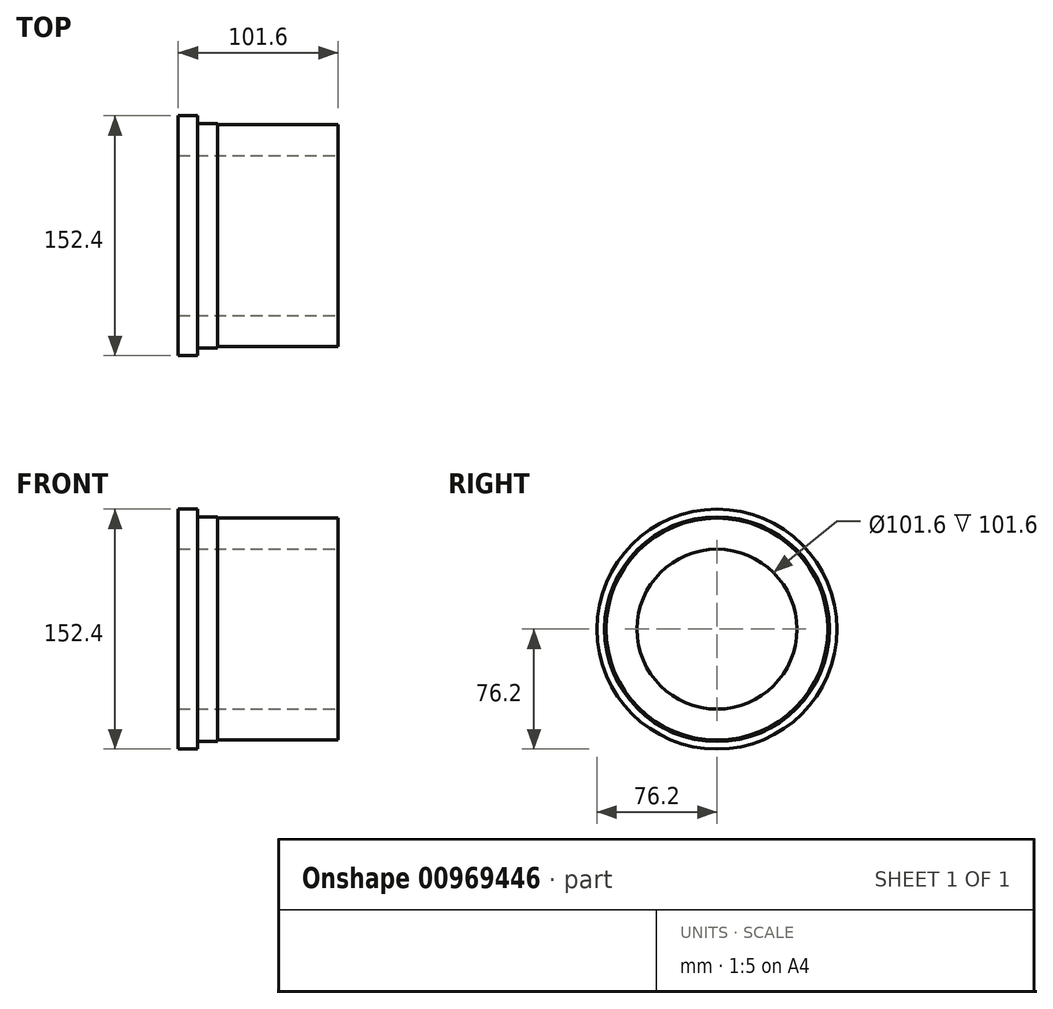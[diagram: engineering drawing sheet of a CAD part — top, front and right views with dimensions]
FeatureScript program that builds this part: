
annotation { "Feature Type Name" : "Feature", "Feature Type Description" : "" }
export const myFeature = defineFeature(function(context is Context, id is Id, definition is map)
    precondition{}
    {
        {
            var Q0;
            Q0=qCreatedBy(makeId("Front.planeOp"),FACE);
            var sketch = newSketch(context, id + "F0", { "sketchPlane" : qUnion([Q0])});
            skLineSegment(sketch, "E0", {"start": v(-17.08, 76.2) * mm, "end": v(-4.77, 76.2) * mm});
            skLineSegment(sketch, "E1", {"start": v(-4.77, 76.2) * mm, "end": v(-4.77, 71.4) * mm});
            skLineSegment(sketch, "E2", {"start": v(-4.77, 71.4) * mm, "end": v(7.93, 71.4) * mm});
            skLineSegment(sketch, "E3", {"start": v(7.93, 70.48) * mm, "end": v(7.93, 71.4) * mm});
            skLineSegment(sketch, "E4", {"start": v(7.93, 70.48) * mm, "end": v(84.52, 70.48) * mm});
            skLineSegment(sketch, "E5", {"start": v(84.52, 70.48) * mm, "end": v(84.52, 50.8) * mm});
            skLineSegment(sketch, "E6", {"start": v(84.52, 50.8) * mm, "end": v(-17.08, 50.8) * mm});
            skLineSegment(sketch, "E7", {"start": v(-17.08, 50.8) * mm, "end": v(-17.08, 76.2) * mm});
            skLineSegment(sketch, "E8", {"start": v(49.98, 0) * mm, "end": v(-59.78, 0) * mm});
            skSolve(sketch);
        }
        {
            var Q0;
            Q0=makeQuery(id+"F0.imprint","IMPRINT",FACE,{"disambiguationData":[TD([[makeQuery(id+"F0.imprint","IMPRINT",EDGE,{"derivedFrom":sQuery(id+"F0.wireOp",EDGE,"E0")}),-1.0]])]});
            var Q1;
            Q1=sQuery(id+"F0.wireOp",EDGE,"E8");
            revolve(context, id + "F1", {"surfaceOperationType" : NewSurfaceOperationType.NEW, "entities" : qUnion([Q0]), "axis" : qUnion([Q1]), "revolveType" : RevolveType.FULL});
        }
    });
